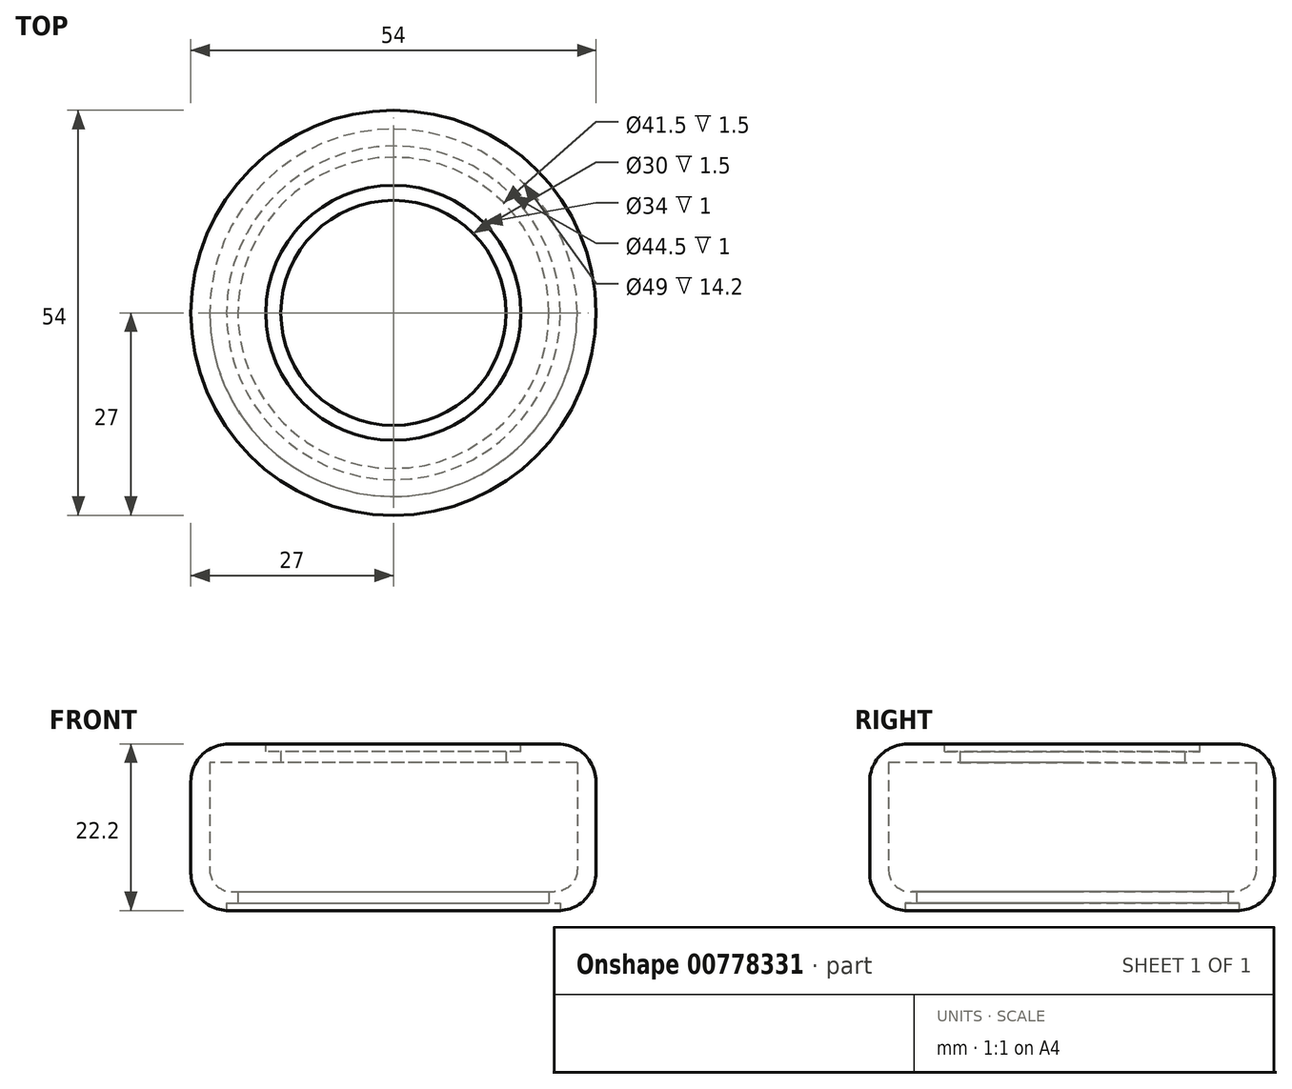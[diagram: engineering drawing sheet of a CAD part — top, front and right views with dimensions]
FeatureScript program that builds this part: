
annotation { "Feature Type Name" : "Feature", "Feature Type Description" : "" }
export const myFeature = defineFeature(function(context is Context, id is Id, definition is map)
    precondition{}
    {
        {
            var Q0;
            Q0=qCreatedBy(makeId("Top.planeOp"),FACE);
            var sketch = newSketch(context, id + "F0", { "sketchPlane" : qUnion([Q0])});
            skCircle(sketch, "E0", {"center": v(0, 0) * mm, "radius": 17 * mm});
            skCircle(sketch, "E1", {"center": v(0, 0) * mm, "radius": 27 * mm});
            skCircle(sketch, "E2", {"center": v(0, 0) * mm, "radius": 15 * mm});
            skSolve(sketch);
        }
        {
            var Q0;
            Q0=makeQuery(id+"F0.imprint","IMPRINT",FACE,{"disambiguationData":[TD([[makeQuery(id+"F0.imprint","IMPRINT",EDGE,{"derivedFrom":sQuery(id+"F0.wireOp",EDGE,"E0")}),-1.0]])]});
            var Q1;
            Q1=makeQuery(id+"F0.imprint","IMPRINT",FACE,{"disambiguationData":[TD([[makeQuery(id+"F0.imprint","IMPRINT",EDGE,{"derivedFrom":sQuery(id+"F0.wireOp",EDGE,"E0")}),1.0]])]});
            extrude(context, id + "F1", {"entities" : qUnion([Q0, Q1]), "depth" : 22.2 * mm, "offsetDistance" : 25 * mm});
        }
        {
            var Q0;
            Q0=makeQuery(id+"F1.opExtrude","CAP_FACE",FACE,{"disambiguationData":[OSD([sQuery(id+"F0.wireOp",EDGE,"E1"),sQuery(id+"F0.wireOp",EDGE,"E2")])],"isStart":false});
            var sketch = newSketch(context, id + "F2", { "sketchPlane" : qUnion([Q0])});
            skCircle(sketch, "E3", {"center": v(0, 0) * mm, "radius": 17 * mm});
            skSolve(sketch);
        }
        {
            var Q0;
            Q0=makeQuery(id+"F2.imprint","IMPRINT",FACE,{"disambiguationData":[TD([[makeQuery(id+"F2.imprint","IMPRINT",EDGE,{"derivedFrom":sQuery(id+"F2.wireOp",EDGE,"E3")}),1.0]])]});
            extrude(context, id + "F3", {"entities" : qUnion([Q0]), "operationType" : NewBodyOperationType.REMOVE, "oppositeDirection" : true, "depth" : 1 * mm, "offsetDistance" : 25 * mm});
        }
        {
            var Q0;
            Q0=makeQuery(id+"F1.opExtrude","CAP_FACE",FACE,{"disambiguationData":[OSD([sQuery(id+"F0.wireOp",EDGE,"E1"),sQuery(id+"F0.wireOp",EDGE,"E2")])],"isStart":true});
            var sketch = newSketch(context, id + "F4", { "sketchPlane" : qUnion([Q0])});
            skCircle(sketch, "E4", {"center": v(0, 0) * mm, "radius": 22.25 * mm});
            skCircle(sketch, "E5", {"center": v(0, 0) * mm, "radius": 20.75 * mm});
            skSolve(sketch);
        }
        {
            var Q0;
            Q0=makeQuery(id+"F4.imprint","IMPRINT",FACE,{"disambiguationData":[TD([[makeQuery(id+"F4.imprint","IMPRINT",EDGE,{"derivedFrom":sQuery(id+"F4.wireOp",EDGE,"E5")}),1.0]])]});
            var Q1;
            Q1=makeQuery(id+"F4.imprint","IMPRINT",FACE,{"disambiguationData":[TD([[makeQuery(id+"F4.imprint","IMPRINT",EDGE,{"derivedFrom":sQuery(id+"F4.wireOp",EDGE,"E4")}),1.0]])]});
            extrude(context, id + "F5", {"entities" : qUnion([Q0, Q1]), "operationType" : NewBodyOperationType.REMOVE, "oppositeDirection" : true, "depth" : 1 * mm, "offsetDistance" : 25 * mm});
        }
        {
            var Q0;
            Q0=makeQuery(id+"F4.imprint","IMPRINT",FACE,{"disambiguationData":[TD([[makeQuery(id+"F4.imprint","IMPRINT",EDGE,{"derivedFrom":sQuery(id+"F4.wireOp",EDGE,"E5")}),1.0]])]});
            extrude(context, id + "F6", {"entities" : qUnion([Q0]), "operationType" : NewBodyOperationType.REMOVE, "oppositeDirection" : true, "depth" : 19.7 * mm, "offsetDistance" : 25 * mm});
        }
        {
            var Q0;
            Q0=makeQuery(id+"F6.boolean.opBoolean","COPY",FACE,{"derivedFrom":makeQuery(id+"F6.opExtrude","SWEPT_FACE",FACE,{"disambiguationData":[OSD([sQuery(id+"F4.wireOp",EDGE,"E5")])]})});
            shell(context, id + "F7", {"entities" : qUnion([Q0]), "thickness" : 2.5 * mm});
        }
        {
            var Q0;
            Q0=makeQuery(id+"F7.opShell","OFFSET_FACE",FACE,{"disambiguationData":[OSD([sQuery(id+"F0.wireOp",EDGE,"E2"),sQuery(id+"F4.wireOp",EDGE,"E4")])]});
            extrude(context, id + "F8", {"entities" : qUnion([Q0]), "operationType" : NewBodyOperationType.REMOVE, "oppositeDirection" : true, "depth" : 1 * mm, "offsetDistance" : 25 * mm});
        }
        {
            var Q0;
            Q0=makeQuery(id+"F1.opExtrude","CAP_EDGE",EDGE,{"disambiguationData":[OSD([sQuery(id+"F0.wireOp",EDGE,"E1")])],"isStart":true});
            var Q1;
            Q1=makeQuery(id+"F1.opExtrude","CAP_EDGE",EDGE,{"disambiguationData":[OSD([sQuery(id+"F0.wireOp",EDGE,"E1")])],"isStart":false});
            fillet(context, id + "F9", {"entities" : qUnion([Q0, Q1]), "radius" : 5 * mm, "tangentPropagation" : true, "allowEdgeOverflow" : false});
        }
        {
            var Q0;
            Q0=makeQuery(id+"F8.boolean.opBoolean","COPY",EDGE,{"derivedFrom":makeQuery(id+"F8.opExtrude","CAP_EDGE",EDGE,{"disambiguationData":[OSD([sQuery(id+"F0.wireOp",EDGE,"E1"),sQuery(id+"F0.wireOp",EDGE,"E2"),sQuery(id+"F4.wireOp",EDGE,"E4")])],"isStart":false})});
            fillet(context, id + "F10", {"entities" : qUnion([Q0]), "radius" : 3 * mm, "tangentPropagation" : true, "allowEdgeOverflow" : false});
        }
    });
